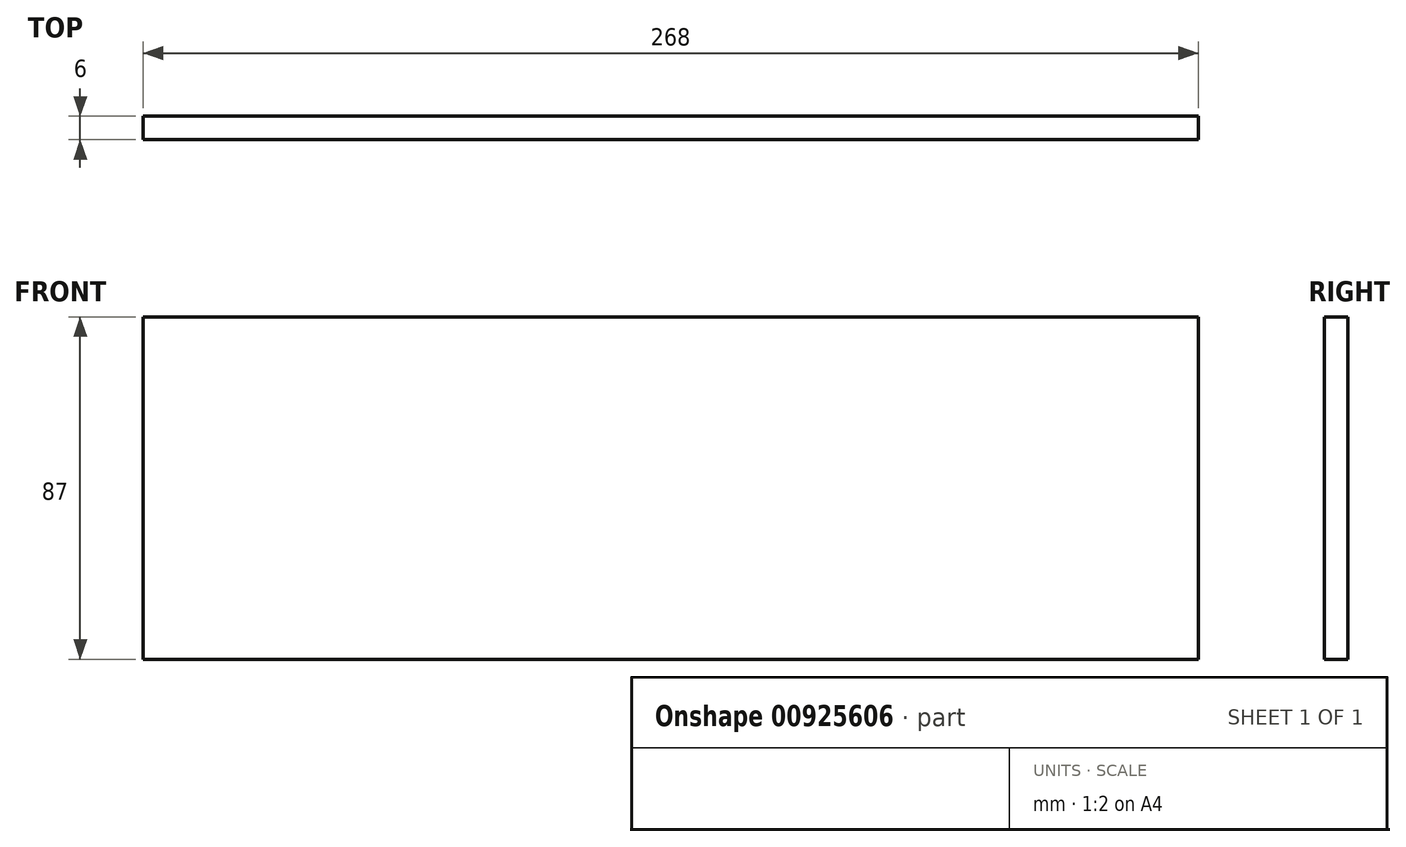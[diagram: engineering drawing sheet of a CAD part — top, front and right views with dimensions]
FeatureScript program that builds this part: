
annotation { "Feature Type Name" : "Feature", "Feature Type Description" : "" }
export const myFeature = defineFeature(function(context is Context, id is Id, definition is map)
    precondition{}
    {
        {
            var Q0;
            Q0=qCreatedBy(makeId("Front.planeOp"),FACE);
            var sketch = newSketch(context, id + "F0", { "sketchPlane" : qUnion([Q0])});
            skLineSegment(sketch, "E0.bottom", {"start": v(134, -43.5) * mm, "end": v(-134, -43.5) * mm});
            skLineSegment(sketch, "E0.top", {"start": v(134, 43.5) * mm, "end": v(22, 43.5) * mm});
            skLineSegment(sketch, "E0.left", {"start": v(134, -43.5) * mm, "end": v(134, 43.5) * mm});
            skLineSegment(sketch, "E0.right", {"start": v(-134, -43.5) * mm, "end": v(-134, 43.5) * mm});
            skLineSegment(sketch, "E1.trimOffspring", {"start": v(-22, 43.5) * mm, "end": v(-134, 43.5) * mm});
            skLineSegment(sketch, "E2", {"start": v(-22, 43.5) * mm, "end": v(22, 43.5) * mm});
            skSolve(sketch);
        }
        {
            var Q0;
            Q0 = qSketchRegion(id + "F0", true);
            extrude(context, id + "F1", {"entities" : qUnion([Q0]), "depth" : 6 * mm, "offsetDistance" : 25 * mm});
        }
    });
